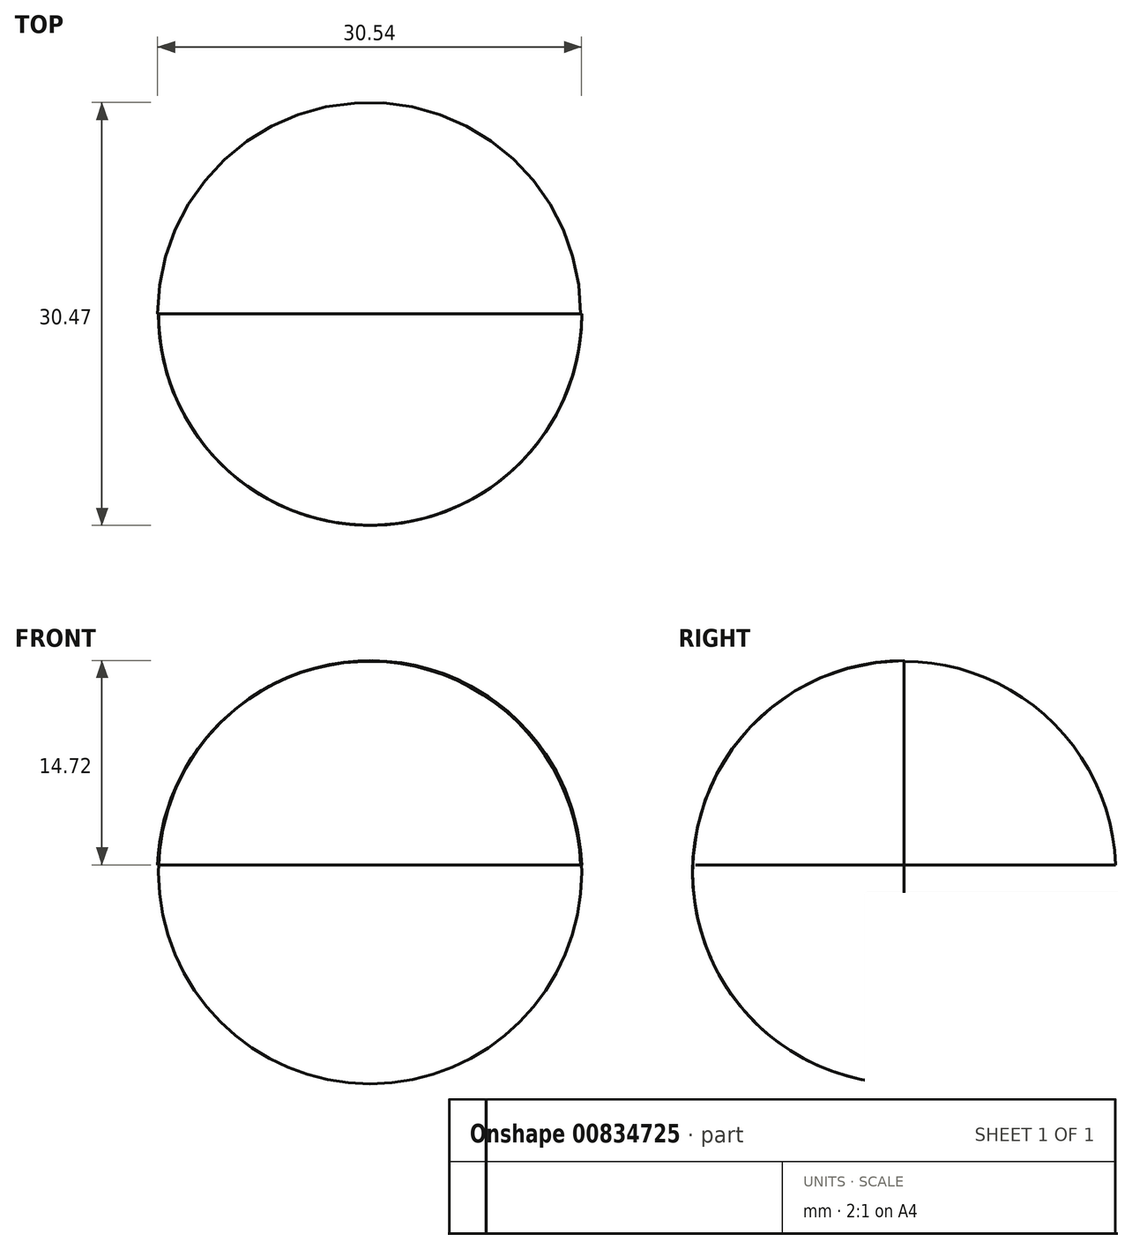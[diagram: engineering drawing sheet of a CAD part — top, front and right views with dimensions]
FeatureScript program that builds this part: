
annotation { "Feature Type Name" : "Feature", "Feature Type Description" : "" }
export const myFeature = defineFeature(function(context is Context, id is Id, definition is map)
    precondition{}
    {
        {
            var Q0;
            Q0=qCreatedBy(makeId("Front.planeOp"),FACE);
            var sketch = newSketch(context, id + "F0", { "sketchPlane" : qUnion([Q0])});
            skArc(sketch, "E0", {"start": v(14.97, 0) * mm, "mid": v(-0.27, 14.72) * mm, "end": v(-15.5, 0) * mm});
            skLineSegment(sketch, "E1", {"start": v(-15.5, 0) * mm, "end": v(14.97, 0) * mm});
            skSolve(sketch);
        }
        {
            var Q0;
            Q0 = qSketchRegion(id + "F0", true);
            extrude(context, id + "F1", {"entities" : qUnion([Q0]), "depth" : 15.24 * mm, "offsetDistance" : 25.4 * mm});
        }
        {
            var Q0;
            Q0=makeQuery(id+"F1.opExtrude","CAP_EDGE",EDGE,{"disambiguationData":[OSD([sQuery(id+"F0.wireOp",EDGE,"E0")])],"isStart":false});
            fillet(context, id + "F2", {"entities" : qUnion([Q0]), "radius" : 15.24 * mm, "tangentPropagation" : true, "allowEdgeOverflow" : false});
        }
        {
            var Q0;
            Q0=qCreatedBy(makeId("Front.planeOp"),FACE);
            var sketch = newSketch(context, id + "F3", { "sketchPlane" : qUnion([Q0])});
            skArc(sketch, "E2", {"start": v(14.9, 0) * mm, "mid": v(-0.33, 14.66) * mm, "end": v(-15.57, 0) * mm});
            skLineSegment(sketch, "E3", {"start": v(14.9, 0) * mm, "end": v(-15.57, 0) * mm});
            skSolve(sketch);
        }
        {
            var Q0;
            Q0 = qSketchRegion(id + "F3", true);
            extrude(context, id + "F4", {"entities" : qUnion([Q0]), "operationType" : NewBodyOperationType.ADD, "oppositeDirection" : true, "depth" : 15.24 * mm, "offsetDistance" : 25.4 * mm});
        }
        {
            var Q0;
            Q0=makeQuery(id+"F4.opExtrude","CAP_EDGE",EDGE,{"disambiguationData":[OSD([sQuery(id+"F3.wireOp",EDGE,"E2")])],"isStart":false});
            fillet(context, id + "F5", {"entities" : qUnion([Q0]), "radius" : 15.24 * mm, "tangentPropagation" : true, "allowEdgeOverflow" : false});
        }
    });
